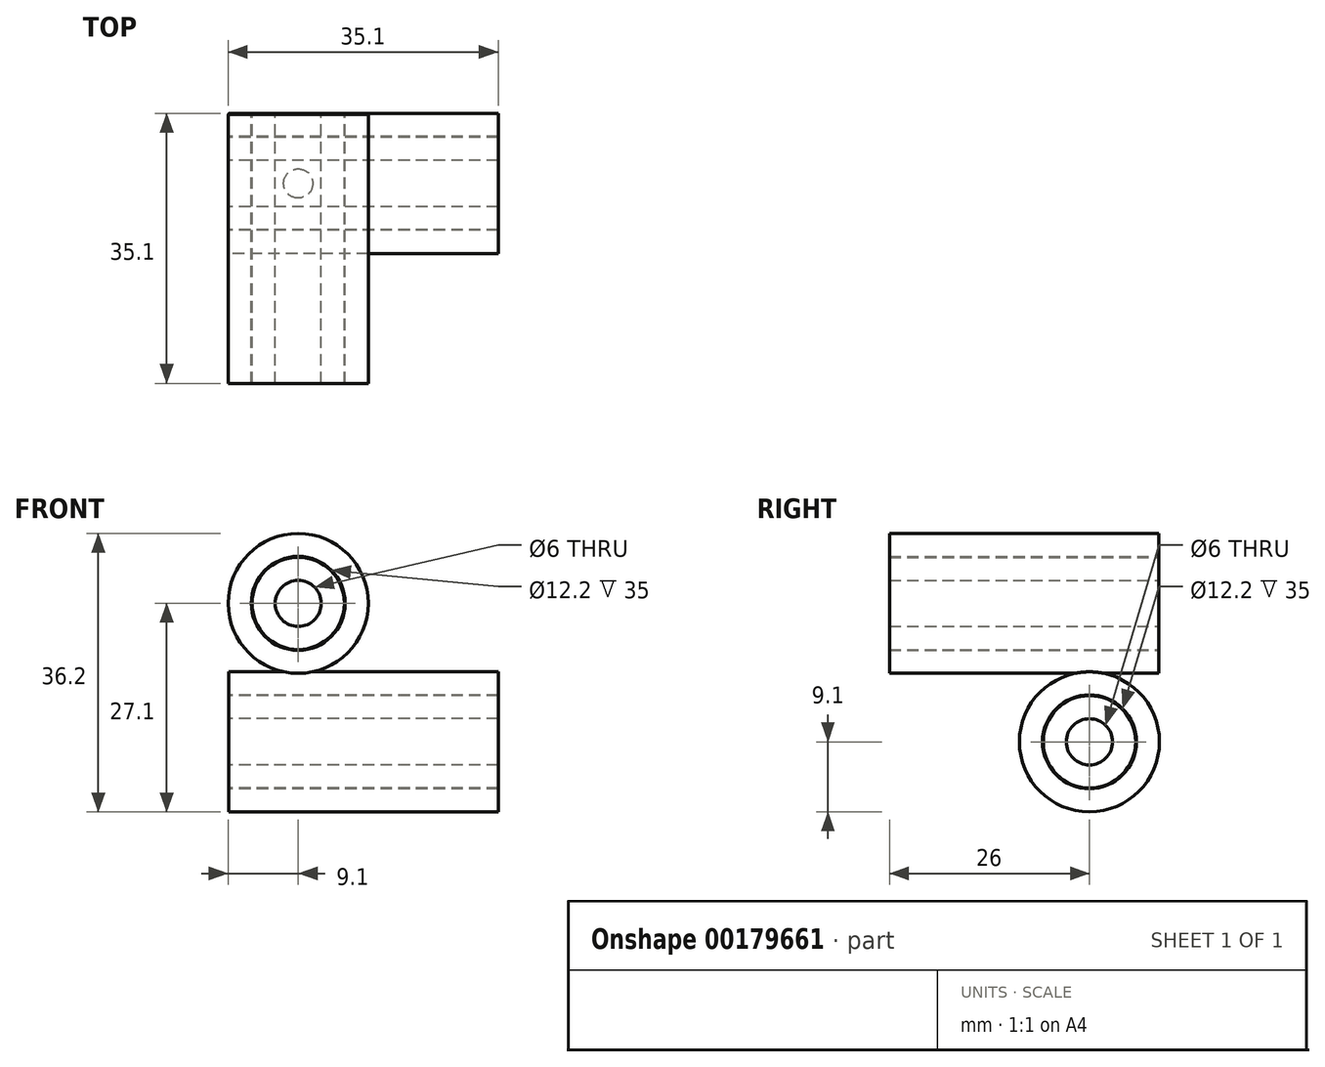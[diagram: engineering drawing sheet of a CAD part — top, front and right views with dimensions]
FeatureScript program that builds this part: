
annotation { "Feature Type Name" : "Feature", "Feature Type Description" : "" }
export const myFeature = defineFeature(function(context is Context, id is Id, definition is map)
    precondition{}
    {
        {
            assignVariable(context, id + "F0", {"name" : "lm6uu_l", "anyValue" : 35});
        }
        {
            var Q0;
            Q0=qCreatedBy(makeId("Front.planeOp"),FACE);
            cPlane(context, id + "F1", {"entities" : qUnion([Q0]), "cplaneType" : CPlaneType.OFFSET, "offset" : 9 * mm, "oppositeDirection" : true, "width" : 150 * mm, "height" : 150 * mm});
        }
        {
            var Q0;
            Q0=qCreatedBy(id+"F1.planeOp",FACE);
            var sketch = newSketch(context, id + "F2", { "sketchPlane" : qUnion([Q0])});
            skCircle(sketch, "E0", {"center": v(0, 50) * mm, "radius": 6 * mm});
            skCircle(sketch, "E1", {"center": v(0, 50) * mm, "radius": 3 * mm});
            skSolve(sketch);
        }
        {
            var Q0;
            Q0=makeQuery(id+"F2.imprint","IMPRINT",FACE,{"disambiguationData":[TD([[makeQuery(id+"F2.imprint","IMPRINT",EDGE,{"derivedFrom":sQuery(id+"F2.wireOp",EDGE,"E0")}),1.0]])]});
            extrude(context, id + "F3", {"entities" : qUnion([Q0]), "depth" : (getVariable(context, 'lm6uu_l')) * mm});
        }
        {
            var Q0;
            Q0=qCreatedBy(makeId("Right.planeOp"),FACE);
            cPlane(context, id + "F4", {"entities" : qUnion([Q0]), "cplaneType" : CPlaneType.OFFSET, "offset" : 9 * mm, "oppositeDirection" : true, "width" : 150 * mm, "height" : 150 * mm});
        }
        {
            var Q0;
            Q0=qCreatedBy(id+"F4.planeOp",FACE);
            var sketch = newSketch(context, id + "F5", { "sketchPlane" : qUnion([Q0])});
            skLineSegment(sketch, "E2", {"start": v(-35, 56) * mm, "end": v(0, 56) * mm, "construction": true});
            skLineSegment(sketch, "E3", {"start": v(0, 44) * mm, "end": v(-35, 44) * mm, "construction": true});
            skLineSegment(sketch, "E4", {"start": v(-47.11, 50) * mm, "end": v(12.64, 50) * mm, "construction": true});
            skCircle(sketch, "E5", {"center": v(0, 32) * mm, "radius": 6 * mm});
            skCircle(sketch, "E6", {"center": v(0, 32) * mm, "radius": 3 * mm});
            skSolve(sketch);
        }
        {
            var Q0;
            Q0=makeQuery(id+"F5.imprint","IMPRINT",FACE,{"disambiguationData":[TD([[makeQuery(id+"F5.imprint","IMPRINT",EDGE,{"derivedFrom":sQuery(id+"F5.wireOp",EDGE,"E5")}),1.0]])]});
            extrude(context, id + "F6", {"entities" : qUnion([Q0]), "depth" : (getVariable(context, 'lm6uu_l')) * mm});
        }
        {
            var Q0;
            Q0=qCreatedBy(id+"F1.planeOp",FACE);
            var sketch = newSketch(context, id + "F7", { "sketchPlane" : qUnion([Q0])});
            skCircle(sketch, "E7.0", {"center": v(0, 50) * mm, "radius": 3 * mm, "construction": true});
            skCircle(sketch, "E8.0", {"center": v(0, 50) * mm, "radius": 6 * mm, "construction": true});
            skCircle(sketch, "E9.0", {"center": v(0, 50) * mm, "radius": 6.1 * mm});
            skCircle(sketch, "E10.0", {"center": v(0, 50) * mm, "radius": 9.1 * mm});
            skSolve(sketch);
        }
        {
            var Q0;
            Q0=qSketchRegion(id+"F7",true);
            extrude(context, id + "F8", {"entities" : qUnion([Q0]), "depth" : (getVariable(context, 'lm6uu_l')) * mm});
        }
        {
            var Q0;
            Q0=qCreatedBy(id+"F4.planeOp",FACE);
            var sketch = newSketch(context, id + "F9", { "sketchPlane" : qUnion([Q0])});
            skCircle(sketch, "E11.0", {"center": v(0, 32) * mm, "radius": 6 * mm});
            skCircle(sketch, "E12.0", {"center": v(0, 32) * mm, "radius": 6.1 * mm});
            skCircle(sketch, "E13.0", {"center": v(0, 32) * mm, "radius": 9.1 * mm});
            skLineSegment(sketch, "E14", {"start": v(-15.96, 32) * mm, "end": v(16.3, 32) * mm, "construction": true});
            skLineSegment(sketch, "E15", {"start": v(-9.1, 32) * mm, "end": v(-9.1, 41.1) * mm});
            skLineSegment(sketch, "E16", {"start": v(-9.1, 41.1) * mm, "end": v(0, 41.1) * mm});
            skLineSegment(sketch, "E17", {"start": v(0, 41.1) * mm, "end": v(9.1, 41.1) * mm});
            skLineSegment(sketch, "E18", {"start": v(9.1, 41.1) * mm, "end": v(9.1, 32) * mm});
            skSolve(sketch);
        }
        {
            var Q0;
            Q0=makeQuery(id+"F9.imprint","IMPRINT",FACE,{"disambiguationData":[TD([[makeQuery(id+"F9.imprint","IMPRINT",EDGE,{"derivedFrom":sQuery(id+"F9.wireOp",EDGE,"E12.0")}),-1.0]])]});
            extrude(context, id + "F10", {"entities" : qUnion([Q0]), "operationType" : NewBodyOperationType.ADD, "depth" : (getVariable(context, 'lm6uu_l')) * mm});
        }
    });
